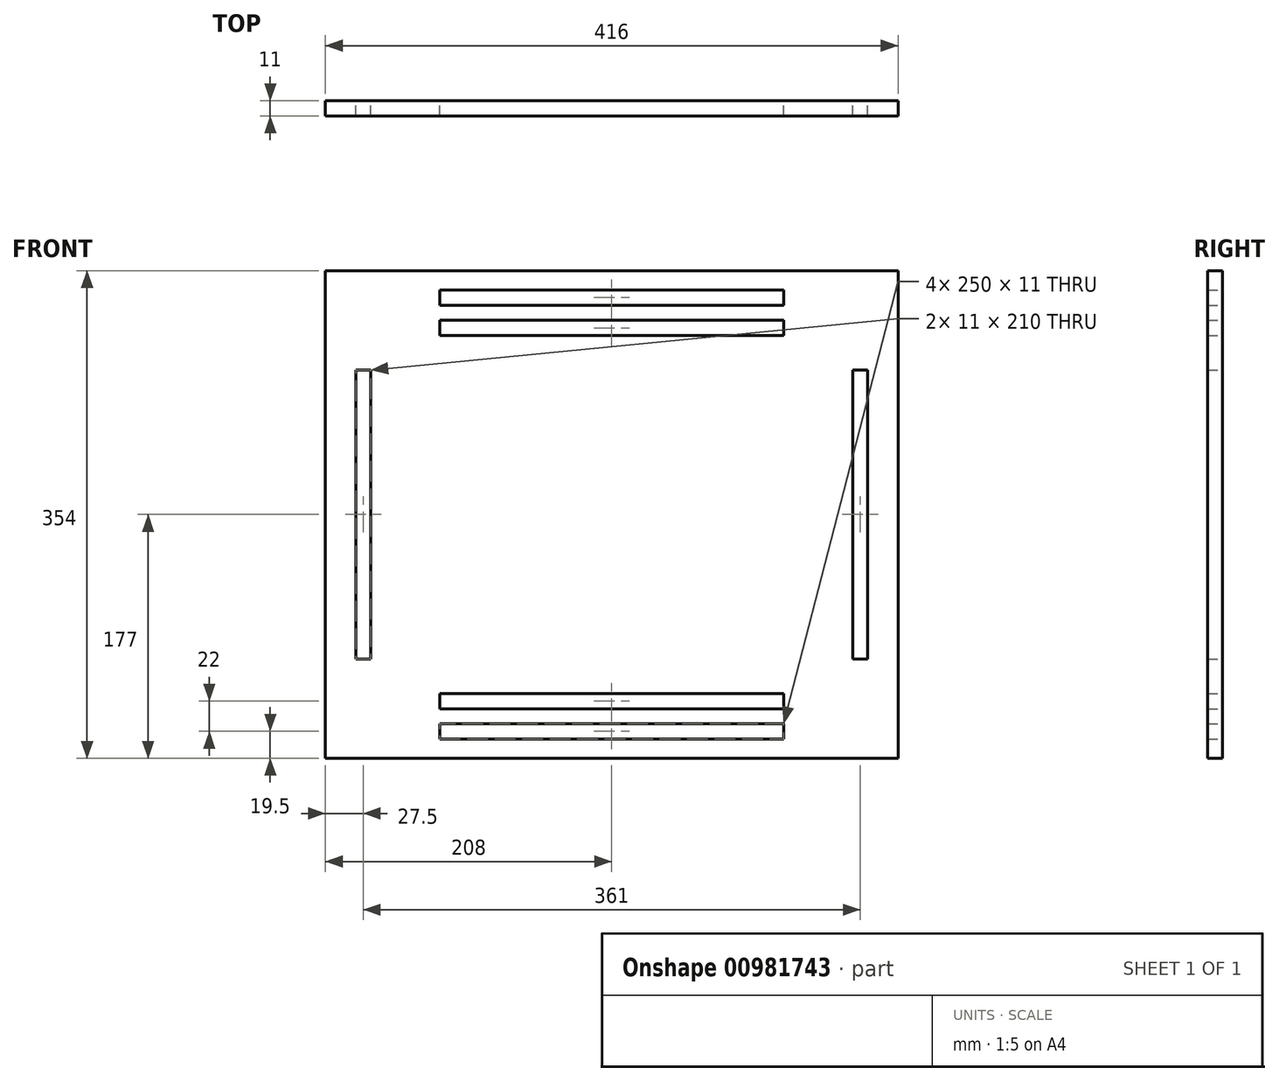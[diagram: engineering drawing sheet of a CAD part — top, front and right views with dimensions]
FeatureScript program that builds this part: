
annotation { "Feature Type Name" : "Feature", "Feature Type Description" : "" }
export const myFeature = defineFeature(function(context is Context, id is Id, definition is map)
    precondition{}
    {
        {
            var Q0;
            Q0=qCreatedBy(makeId("Front.planeOp"),FACE);
            var sketch = newSketch(context, id + "F0", { "sketchPlane" : qUnion([Q0])});
            skLineSegment(sketch, "E0", {"start": v(208, 177) * mm, "end": v(208, -177) * mm});
            skLineSegment(sketch, "E1", {"start": v(-208, 177) * mm, "end": v(-208, -177) * mm});
            skLineSegment(sketch, "E2", {"start": v(208, 177) * mm, "end": v(-208, 177) * mm});
            skLineSegment(sketch, "E3", {"start": v(208, -177) * mm, "end": v(-208, -177) * mm});
            skLineSegment(sketch, "E4", {"start": v(125, -141) * mm, "end": v(-125, -141) * mm});
            skLineSegment(sketch, "E5", {"start": v(125, -130) * mm, "end": v(-125, -130) * mm});
            skLineSegment(sketch, "E6", {"start": v(125, 130) * mm, "end": v(-125, 130) * mm});
            skLineSegment(sketch, "E7", {"start": v(125, 141) * mm, "end": v(-125, 141) * mm});
            skLineSegment(sketch, "E8", {"start": v(-175, -105) * mm, "end": v(-175, 105) * mm});
            skLineSegment(sketch, "E9", {"start": v(-125, -141) * mm, "end": v(-125, -130) * mm});
            skLineSegment(sketch, "E10", {"start": v(-125, 130) * mm, "end": v(-125, 141) * mm});
            skLineSegment(sketch, "E11", {"start": v(-186, -105) * mm, "end": v(-186, 105) * mm});
            skLineSegment(sketch, "E12", {"start": v(175, -105) * mm, "end": v(175, 105) * mm});
            skLineSegment(sketch, "E13", {"start": v(125, -141) * mm, "end": v(125, -130) * mm});
            skLineSegment(sketch, "E14", {"start": v(125, 130) * mm, "end": v(125, 141) * mm});
            skLineSegment(sketch, "E15", {"start": v(186, -105) * mm, "end": v(186, 105) * mm});
            skLineSegment(sketch, "E16", {"start": v(-186, 105) * mm, "end": v(-175, 105) * mm});
            skLineSegment(sketch, "E17", {"start": v(175, 105) * mm, "end": v(186, 105) * mm});
            skLineSegment(sketch, "E18", {"start": v(-186, -105) * mm, "end": v(-175, -105) * mm});
            skLineSegment(sketch, "E19", {"start": v(175, -105) * mm, "end": v(186, -105) * mm});
            skLineSegment(sketch, "E20", {"start": v(125, 152) * mm, "end": v(-125, 152) * mm});
            skLineSegment(sketch, "E21", {"start": v(125, 163) * mm, "end": v(-125, 163) * mm});
            skLineSegment(sketch, "E22", {"start": v(-125, 152) * mm, "end": v(-125, 163) * mm});
            skLineSegment(sketch, "E23", {"start": v(125, 152) * mm, "end": v(125, 163) * mm});
            skLineSegment(sketch, "E24", {"start": v(125, -163) * mm, "end": v(-125, -163) * mm});
            skLineSegment(sketch, "E25", {"start": v(125, -152) * mm, "end": v(-125, -152) * mm});
            skLineSegment(sketch, "E26", {"start": v(-125, -163) * mm, "end": v(-125, -152) * mm});
            skLineSegment(sketch, "E27", {"start": v(125, -163) * mm, "end": v(125, -152) * mm});
            skSolve(sketch);
        }
        {
            var Q0;
            Q0=makeQuery(id+"F0.imprint","IMPRINT",FACE,{"disambiguationData":[TD([[makeQuery(id+"F0.imprint","IMPRINT",EDGE,{"derivedFrom":sQuery(id+"F0.wireOp",EDGE,"E0")}),-1.0]])]});
            extrude(context, id + "F1", {"entities" : qUnion([Q0]), "depth" : 11 * mm, "offsetDistance" : 25 * mm});
        }
    });
